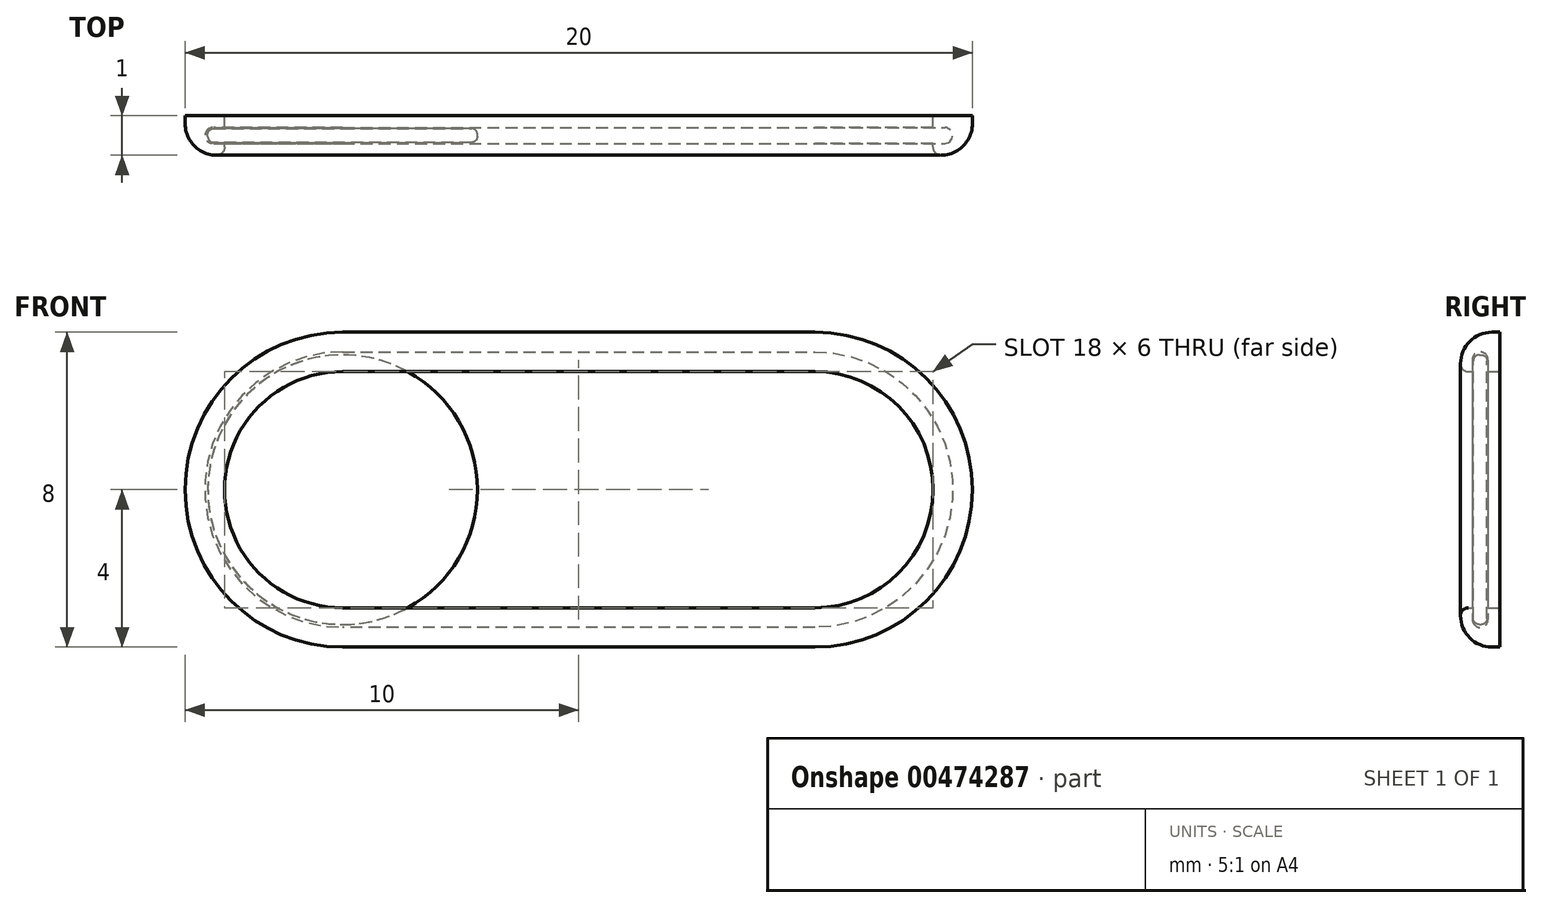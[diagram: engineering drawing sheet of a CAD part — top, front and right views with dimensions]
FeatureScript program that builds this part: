
annotation { "Feature Type Name" : "Feature", "Feature Type Description" : "" }
export const myFeature = defineFeature(function(context is Context, id is Id, definition is map)
    precondition{}
    {
        {
            var Q0;
            Q0=qCreatedBy(makeId("Front.planeOp"),FACE);
            var sketch = newSketch(context, id + "F0", { "sketchPlane" : qUnion([Q0])});
            skLineSegment(sketch, "E0.bottom", {"start": v(-6, 3) * mm, "end": v(6, 3) * mm});
            skLineSegment(sketch, "E0.top", {"start": v(-6, -3) * mm, "end": v(6, -3) * mm});
            skPoint(sketch, "E0.middle", {"position": v(0, 0) * mm});
            skArc(sketch, "E1", {"start": v(-6, 3) * mm, "mid": v(-9, 0) * mm, "end": v(-6, -3) * mm});
            skArc(sketch, "E2", {"start": v(6, 3) * mm, "mid": v(9, 0) * mm, "end": v(6, -3) * mm});
            skLineSegment(sketch, "E3.0", {"start": v(-6, 4) * mm, "end": v(6, 4) * mm});
            skArc(sketch, "E3.1", {"start": v(-6, 4) * mm, "mid": v(-10, 0) * mm, "end": v(-6, -4) * mm});
            skLineSegment(sketch, "E3.2", {"start": v(-6, -4) * mm, "end": v(6, -4) * mm});
            skArc(sketch, "E3.3", {"start": v(6, 4) * mm, "mid": v(10, 0) * mm, "end": v(6, -4) * mm});
            skLineSegment(sketch, "E4.0", {"start": v(-6, 3.5) * mm, "end": v(6, 3.5) * mm});
            skArc(sketch, "E4.1", {"start": v(-6, 3.5) * mm, "mid": v(-9.5, 0) * mm, "end": v(-6, -3.5) * mm});
            skLineSegment(sketch, "E4.2", {"start": v(-6, -3.5) * mm, "end": v(6, -3.5) * mm});
            skArc(sketch, "E4.3", {"start": v(6, 3.5) * mm, "mid": v(9.5, 0) * mm, "end": v(6, -3.5) * mm});
            skLineSegment(sketch, "E5.0", {"start": v(-6, 2.75) * mm, "end": v(6, 2.75) * mm, "construction": true});
            skArc(sketch, "E5.1", {"start": v(-6, 2.75) * mm, "mid": v(-8.75, 0) * mm, "end": v(-6, -2.75) * mm, "construction": true});
            skLineSegment(sketch, "E5.2", {"start": v(-6, -2.75) * mm, "end": v(6, -2.75) * mm, "construction": true});
            skArc(sketch, "E5.3", {"start": v(6, 2.75) * mm, "mid": v(8.75, 0) * mm, "end": v(6, -2.75) * mm, "construction": true});
            skSolve(sketch);
        }
        {
            var Q0;
            Q0=makeQuery(id+"F0.imprint","IMPRINT",FACE,{"disambiguationData":[TD([[makeQuery(id+"F0.imprint","IMPRINT",EDGE,{"derivedFrom":sQuery(id+"F0.wireOp",EDGE,"E0.bottom")}),1.0]])]});
            var Q1;
            Q1=makeQuery(id+"F0.imprint","IMPRINT",FACE,{"disambiguationData":[TD([[makeQuery(id+"F0.imprint","IMPRINT",EDGE,{"derivedFrom":sQuery(id+"F0.wireOp",EDGE,"E3.0")}),-1.0]])]});
            extrude(context, id + "F1", {"entities" : qUnion([Q0, Q1]), "endBound" : BoundingType.SYMMETRIC, "depth" : 1 * mm});
        }
        {
            var Q0;
            Q0=makeQuery(id+"F0.imprint","IMPRINT",FACE,{"disambiguationData":[TD([[makeQuery(id+"F0.imprint","IMPRINT",EDGE,{"derivedFrom":sQuery(id+"F0.wireOp",EDGE,"E0.bottom")}),1.0]])]});
            var Q1;
            Q1=makeQuery(id+"F0.imprint","IMPRINT",FACE,{"disambiguationData":[TD([[makeQuery(id+"F0.imprint","IMPRINT",EDGE,{"derivedFrom":sQuery(id+"F0.wireOp",EDGE,"E0.bottom")}),-1.0]])]});
            extrude(context, id + "F2", {"entities" : qUnion([Q0, Q1]), "operationType" : NewBodyOperationType.REMOVE, "endBound" : BoundingType.SYMMETRIC, "oppositeDirection" : true, "depth" : .4 * mm});
        }
        {
            var Q0;
            Q0=makeQuery(id+"F2.boolean.opBoolean","COPY",EDGE,{"derivedFrom":makeQuery(id+"F2.opExtrude","CAP_EDGE",EDGE,{"disambiguationData":[OSD([sQuery(id+"F0.wireOp",EDGE,"E4.0")])],"isStart":true})});
            var Q1;
            Q1=makeQuery(id+"F2.boolean.opBoolean","COPY",EDGE,{"derivedFrom":makeQuery(id+"F2.opExtrude","CAP_EDGE",EDGE,{"disambiguationData":[OSD([sQuery(id+"F0.wireOp",EDGE,"E4.3")])],"isStart":true})});
            var Q2;
            Q2=makeQuery(id+"F2.boolean.opBoolean","COPY",EDGE,{"derivedFrom":makeQuery(id+"F2.opExtrude","CAP_EDGE",EDGE,{"disambiguationData":[OSD([sQuery(id+"F0.wireOp",EDGE,"E4.0")])],"isStart":false})});
            var Q3;
            Q3=makeQuery(id+"F2.boolean.opBoolean","COPY",EDGE,{"derivedFrom":makeQuery(id+"F2.opExtrude","CAP_EDGE",EDGE,{"disambiguationData":[OSD([sQuery(id+"F0.wireOp",EDGE,"E4.3")])],"isStart":false})});
            var Q4;
            Q4=makeQuery(id+"F2.boolean.opBoolean","COPY",EDGE,{"derivedFrom":makeQuery(id+"F2.opExtrude","CAP_EDGE",EDGE,{"disambiguationData":[OSD([sQuery(id+"F0.wireOp",EDGE,"E4.2")])],"isStart":false})});
            var Q5;
            Q5=makeQuery(id+"F2.boolean.opBoolean","COPY",EDGE,{"derivedFrom":makeQuery(id+"F2.opExtrude","CAP_EDGE",EDGE,{"disambiguationData":[OSD([sQuery(id+"F0.wireOp",EDGE,"E4.2")])],"isStart":true})});
            var Q6;
            Q6=makeQuery(id+"F2.boolean.opBoolean","COPY",EDGE,{"derivedFrom":makeQuery(id+"F2.opExtrude","CAP_EDGE",EDGE,{"disambiguationData":[OSD([sQuery(id+"F0.wireOp",EDGE,"E4.1")])],"isStart":false})});
            var Q7;
            Q7=makeQuery(id+"F2.boolean.opBoolean","COPY",EDGE,{"derivedFrom":makeQuery(id+"F2.opExtrude","CAP_EDGE",EDGE,{"disambiguationData":[OSD([sQuery(id+"F0.wireOp",EDGE,"E4.1")])],"isStart":true})});
            fillet(context, id + "F3", {"entities" : qUnion([Q0, Q1, Q2, Q3, Q4, Q5, Q6, Q7]), "radius" : .2 * mm, "tangentPropagation" : true, "allowEdgeOverflow" : false});
        }
        {
            var Q0;
            Q0=makeQuery(id+"F1.opExtrude","CAP_EDGE",EDGE,{"disambiguationData":[OSD([sQuery(id+"F0.wireOp",EDGE,"E3.1")])],"isStart":false});
            var Q1;
            Q1=makeQuery(id+"F1.opExtrude","CAP_EDGE",EDGE,{"disambiguationData":[OSD([sQuery(id+"F0.wireOp",EDGE,"E3.0")])],"isStart":false});
            var Q2;
            Q2=makeQuery(id+"F1.opExtrude","CAP_EDGE",EDGE,{"disambiguationData":[OSD([sQuery(id+"F0.wireOp",EDGE,"E3.3")])],"isStart":false});
            var Q3;
            Q3=makeQuery(id+"F1.opExtrude","CAP_EDGE",EDGE,{"disambiguationData":[OSD([sQuery(id+"F0.wireOp",EDGE,"E3.2")])],"isStart":false});
            fillet(context, id + "F4", {"entities" : qUnion([Q0, Q1, Q2, Q3]), "radius" : .8 * mm, "tangentPropagation" : true, "allowEdgeOverflow" : false});
        }
        {
            var Q0;
            Q0=makeQuery(id+"F0.imprint","IMPRINT",FACE,{"disambiguationData":[TD([[makeQuery(id+"F0.imprint","IMPRINT",EDGE,{"derivedFrom":sQuery(id+"F0.wireOp",EDGE,"E0.bottom")}),-1.0]])]});
            var sketch = newSketch(context, id + "F5", { "sketchPlane" : qUnion([Q0])});
            skCircle(sketch, "E6", {"center": v(-6, 0) * mm, "radius": 3.43 * mm});
            skSolve(sketch);
        }
        {
            var Q0;
            Q0 = qSketchRegion(id + "F5", true);
            extrude(context, id + "F6", {"entities" : qUnion([Q0]), "endBound" : BoundingType.SYMMETRIC, "depth" : .35 * mm});
        }
        {
            var Q0;
            Q0=makeQuery(id+"F6.opExtrude","CAP_EDGE",EDGE,{"disambiguationData":[OSD([sQuery(id+"F5.wireOp",EDGE,"E6")])],"isStart":false});
            var Q1;
            Q1=makeQuery(id+"F6.opExtrude","CAP_EDGE",EDGE,{"disambiguationData":[OSD([sQuery(id+"F5.wireOp",EDGE,"E6")])],"isStart":true});
            fillet(context, id + "F7", {"entities" : qUnion([Q0, Q1]), "radius" : .15 * mm, "tangentPropagation" : true, "allowEdgeOverflow" : false});
        }
        {
            var Q0;
            Q0=makeQuery(id+"F1.opExtrude","CAP_EDGE",EDGE,{"disambiguationData":[OSD([sQuery(id+"F0.wireOp",EDGE,"E0.bottom")])],"isStart":false});
            var Q1;
            Q1=makeQuery(id+"F1.opExtrude","CAP_EDGE",EDGE,{"disambiguationData":[OSD([sQuery(id+"F0.wireOp",EDGE,"E1")])],"isStart":false});
            var Q2;
            Q2=makeQuery(id+"F1.opExtrude","CAP_EDGE",EDGE,{"disambiguationData":[OSD([sQuery(id+"F0.wireOp",EDGE,"E0.top")])],"isStart":false});
            var Q3;
            Q3=makeQuery(id+"F1.opExtrude","CAP_EDGE",EDGE,{"disambiguationData":[OSD([sQuery(id+"F0.wireOp",EDGE,"E2")])],"isStart":false});
            fillet(context, id + "F8", {"entities" : qUnion([Q0, Q1, Q2, Q3]), "radius" : .2 * mm, "tangentPropagation" : true, "allowEdgeOverflow" : false});
        }
    });
